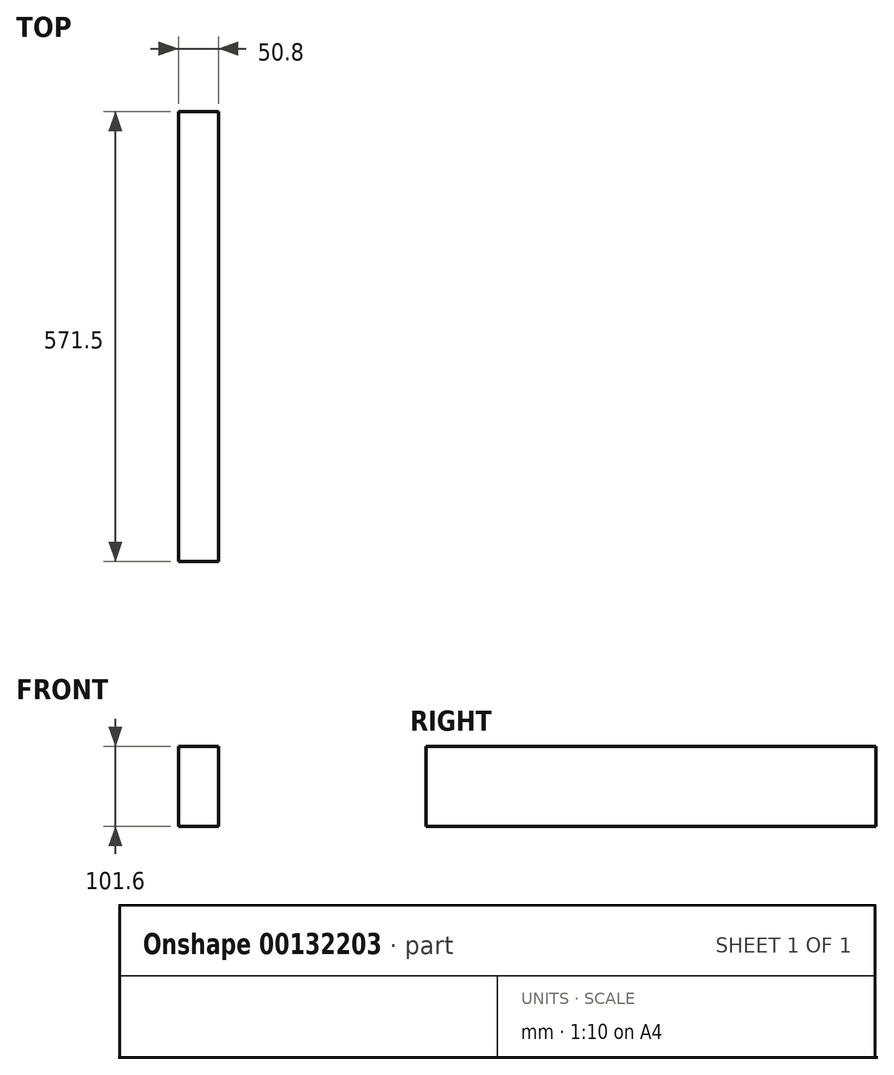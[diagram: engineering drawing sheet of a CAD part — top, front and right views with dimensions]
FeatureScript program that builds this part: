
annotation { "Feature Type Name" : "Feature", "Feature Type Description" : "" }
export const myFeature = defineFeature(function(context is Context, id is Id, definition is map)
    precondition{}
    {
        {
            var Q0;
            Q0=qCreatedBy(makeId("Right.planeOp"),FACE);
            var sketch = newSketch(context, id + "F0", { "sketchPlane" : qUnion([Q0])});
            skLineSegment(sketch, "E0.bottom", {"start": v(-285.75, -50.8) * mm, "end": v(285.75, -50.8) * mm});
            skLineSegment(sketch, "E0.top", {"start": v(-285.75, 50.8) * mm, "end": v(285.75, 50.8) * mm});
            skLineSegment(sketch, "E0.left", {"start": v(-285.75, -50.8) * mm, "end": v(-285.75, 50.8) * mm});
            skLineSegment(sketch, "E0.right", {"start": v(285.75, -50.8) * mm, "end": v(285.75, 50.8) * mm});
            skPoint(sketch, "E0.middle", {"position": v(0, 0) * mm});
            skSolve(sketch);
        }
        {
            var Q0;
            Q0=makeQuery(id+"F0.imprint","IMPRINT",FACE,{"disambiguationData":[TD([[makeQuery(id+"F0.imprint","IMPRINT",EDGE,{"derivedFrom":sQuery(id+"F0.wireOp",EDGE,"E0.bottom")}),1.0]])]});
            extrude(context, id + "F1", {"entities" : qUnion([Q0]), "endBound" : BoundingType.SYMMETRIC, "depth" : 50.8 * mm});
        }
    });
